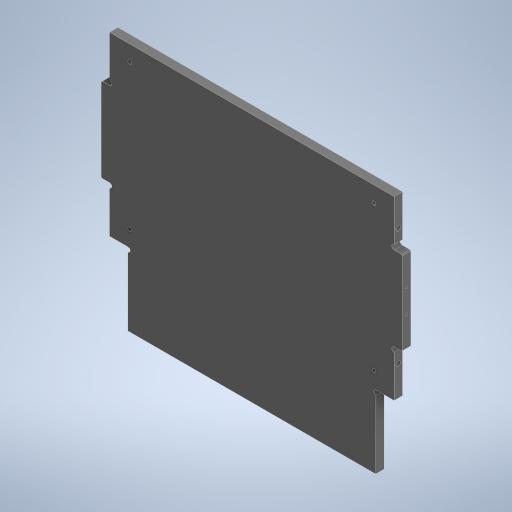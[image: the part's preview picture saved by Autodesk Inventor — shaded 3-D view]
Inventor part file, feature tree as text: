
AUTODESK INVENTOR PART (.ipt)
format: ipt  version: 2024.2 (Build 282272000, 272)  size: 327,168 bytes
history: native  units: mm
features: sketch x3, hole x2, extrude x1, chamfer x1
ambient origin geometry x8: Origin, YZ Plane, XZ Plane, XY Plane, X Axis, Y Axis, Z Axis, Center Point
bodies: Solid1 (feature_tree)
feature tree (7):
  sketch  "Sketch1"  dims[d0=180.0mm d1=149.0mm]
  extrude  "Extrusion1"  Depth=149.0mm
  hole  "Side-M2"  [1 undecoded]
  hole  "Phi3.0"  [1 undecoded]
  chamfer  "C0.5"  Distance=4.2mm
  sketch  "Sketch2"  dims[d2=1.5mm d3=5.0mm]
  sketch  "Sketch3"  dims[d5=5.0mm d6=0.0mm d8=1.567mm d9=4.0mm d10=4.0mm d11=2.0mm d12=90.0deg d13=5.0mm d14=0.0mm d15=6.0mm d16=4.2mm d17=9.0mm d18=5.0mm d20=2.459mm d21=6.0mm d22=4.0mm d23=2.0mm d24=90.0deg d25=8.8mm d26=0.0mm d27=5.0mm d28=14.0mm d38=50.0mm d40=52.75mm d41=0.5mm d42=2.0mm d43=45.0deg d44=11.0mm d45=43.5mm d46=5.0mm d47=105.5mm d48=70.0mm d49=3.0mm d50=6.0mm d51=4.0mm d52=2.0mm d53=90.0deg d54=6.0mm d55=0.0mm]
note: 2 required parameter values undecoded (feature->parameter linkage not recoverable at this tier; creation-order binding heuristic only, values carry confidence <= 0.55)
